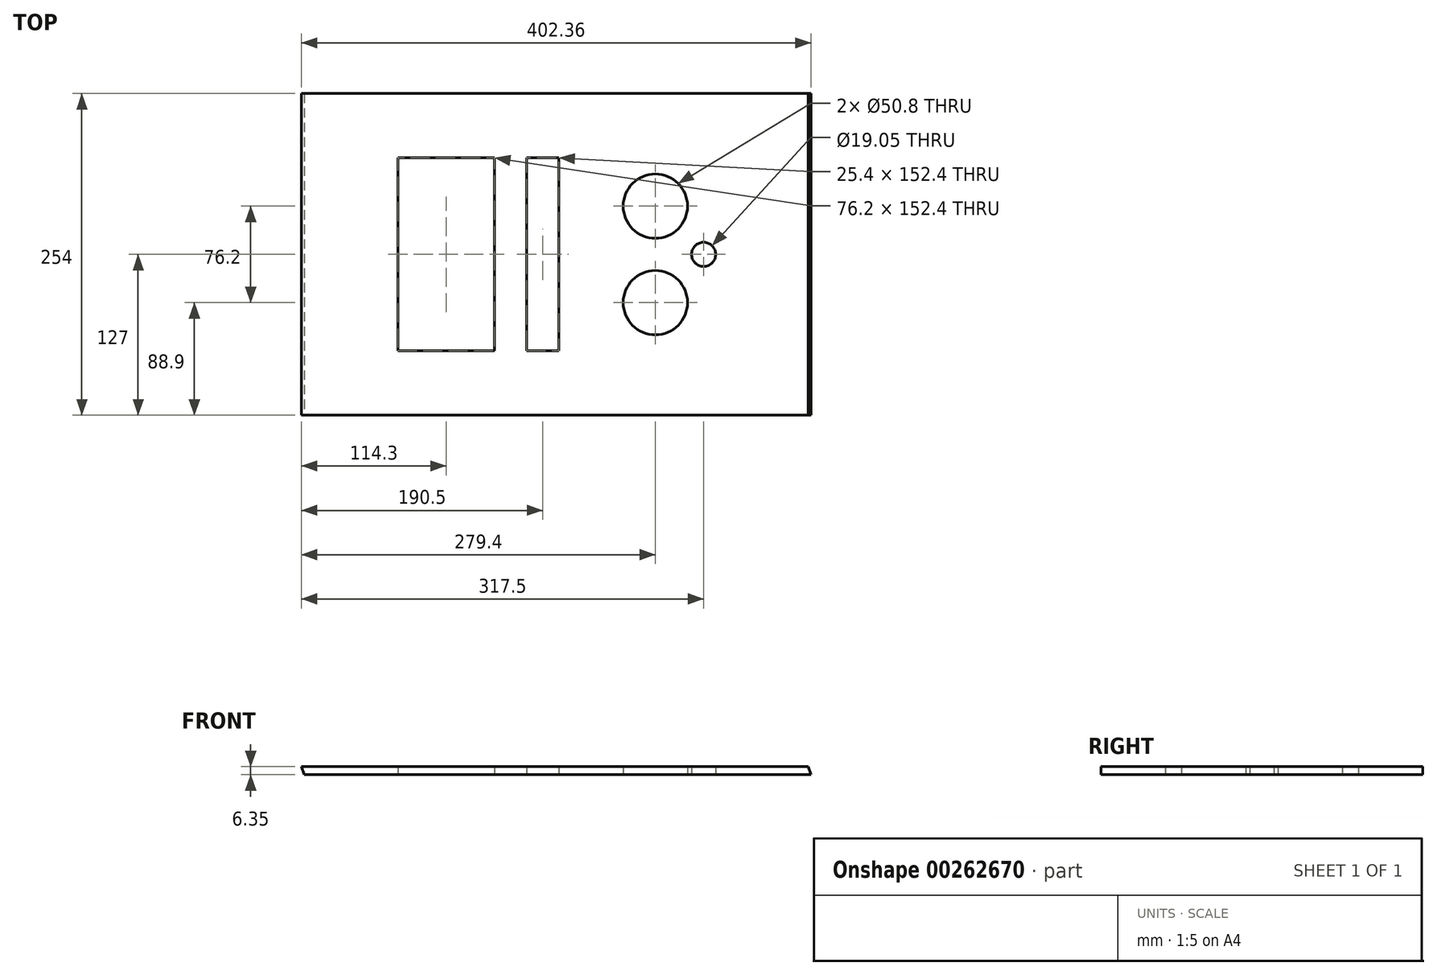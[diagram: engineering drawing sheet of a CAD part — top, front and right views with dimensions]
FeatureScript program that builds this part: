
annotation { "Feature Type Name" : "Feature", "Feature Type Description" : "" }
export const myFeature = defineFeature(function(context is Context, id is Id, definition is map)
    precondition{}
    {
        {
            var Q0;
            Q0=qCreatedBy(makeId("Top.planeOp"),FACE);
            var sketch = newSketch(context, id + "F0", { "sketchPlane" : qUnion([Q0])});
            skLineSegment(sketch, "E0.bottom", {"start": v(0, 0) * mm, "end": v(406.4, 0) * mm});
            skLineSegment(sketch, "E0.top", {"start": v(0, 254) * mm, "end": v(406.4, 254) * mm});
            skLineSegment(sketch, "E0.left", {"start": v(0, 0) * mm, "end": v(0, 254) * mm});
            skLineSegment(sketch, "E0.right", {"start": v(406.4, 0) * mm, "end": v(406.4, 254) * mm});
            skLineSegment(sketch, "E1.bottom", {"start": v(76.2, 203.2) * mm, "end": v(152.4, 203.2) * mm});
            skLineSegment(sketch, "E1.top", {"start": v(76.2, 50.8) * mm, "end": v(152.4, 50.8) * mm});
            skLineSegment(sketch, "E1.left", {"start": v(76.2, 203.2) * mm, "end": v(76.2, 50.8) * mm});
            skLineSegment(sketch, "E1.right", {"start": v(152.4, 203.2) * mm, "end": v(152.4, 50.8) * mm});
            skLineSegment(sketch, "E2.bottom", {"start": v(177.8, 203.2) * mm, "end": v(203.2, 203.2) * mm});
            skLineSegment(sketch, "E2.top", {"start": v(177.8, 50.8) * mm, "end": v(203.2, 50.8) * mm});
            skLineSegment(sketch, "E2.left", {"start": v(177.8, 203.2) * mm, "end": v(177.8, 50.8) * mm});
            skLineSegment(sketch, "E2.right", {"start": v(203.2, 203.2) * mm, "end": v(203.2, 50.8) * mm});
            skCircle(sketch, "E3", {"center": v(279.4, 88.9) * mm, "radius": 25.4 * mm});
            skCircle(sketch, "E4", {"center": v(279.4, 165.1) * mm, "radius": 25.4 * mm});
            skCircle(sketch, "E5", {"center": v(317.5, 127) * mm, "radius": 9.53 * mm});
            skPoint(sketch, "E5.centerSnap0", {"position": v(203.2, 127) * mm});
            skSolve(sketch);
        }
        {
            var Q0;
            Q0=makeQuery(id+"F0.imprint","IMPRINT",FACE,{"disambiguationData":[TD([[makeQuery(id+"F0.imprint","IMPRINT",EDGE,{"derivedFrom":sQuery(id+"F0.wireOp",EDGE,"E0.bottom")}),1.0]])]});
            extrude(context, id + "F1", {"entities" : qUnion([Q0]), "depth" : 6.35 * mm});
        }
        {
            var Q0;
            Q0=makeQuery(id+"F1.opExtrude","SWEPT_FACE",FACE,{"disambiguationData":[OSD([sQuery(id+"F0.wireOp",EDGE,"E0.bottom")])]});
            var sketch = newSketch(context, id + "F2", { "sketchPlane" : qUnion([Q0])});
            skLineSegment(sketch, "E6", {"start": v(-1.79, 11.26) * mm, "end": v(2.31, 0) * mm});
            skLineSegment(sketch, "E7", {"start": v(2.31, 0) * mm, "end": v(-1.79, 0) * mm});
            skLineSegment(sketch, "E8", {"start": v(-1.79, 0) * mm, "end": v(-1.79, 11.26) * mm});
            skSolve(sketch);
        }
        {
            var Q0;
            {var subQ1=sQuery(id+"F0.wireOp",EDGE,"E0.bottom");var subQ2=makeQuery(id+"F1.opExtrude","SWEPT_EDGE",EDGE,{"disambiguationData":[OSD([subQ1,sQuery(id+"F0.wireOp",EDGE,"E0.left")])]});Q0=makeQuery(id+"F2.imprint","IMPRINT",FACE,{"disambiguationData":[TD([[makeQuery(id+"F2.imprint","IMPRINT",EDGE,{"derivedFrom":subQ2}),1.0]])]});}
            extrude(context, id + "F3", {"entities" : qUnion([Q0]), "operationType" : NewBodyOperationType.REMOVE, "endBound" : BoundingType.THROUGH_ALL, "oppositeDirection" : true, "depth" : 25.4 * mm});
        }
        {
            var Q0;
            Q0=makeQuery(id+"F1.opExtrude","SWEPT_FACE",FACE,{"disambiguationData":[OSD([sQuery(id+"F0.wireOp",EDGE,"E0.bottom")])]});
            var sketch = newSketch(context, id + "F4", { "sketchPlane" : qUnion([Q0])});
            skLineSegment(sketch, "E9", {"start": v(2.31, 0) * mm, "end": v(402.36, 0) * mm});
            skLineSegment(sketch, "E10", {"start": v(402.36, 0) * mm, "end": v(396.66, 15.66) * mm});
            skLineSegment(sketch, "E11", {"start": v(396.66, 15.66) * mm, "end": v(417.73, 15.66) * mm});
            skLineSegment(sketch, "E12", {"start": v(417.73, 15.66) * mm, "end": v(417.73, 0) * mm});
            skLineSegment(sketch, "E13", {"start": v(417.73, 0) * mm, "end": v(402.36, 0) * mm});
            skSolve(sketch);
        }
        {
            var Q0;
            {var subQ3=sQuery(id+"F0.wireOp",EDGE,"E0.bottom");var subQ6=makeQuery(id+"F1.opExtrude","SWEPT_EDGE",EDGE,{"disambiguationData":[OSD([subQ3,sQuery(id+"F0.wireOp",EDGE,"E0.right")])]});Q0=makeQuery(id+"F4.imprint","IMPRINT",FACE,{"disambiguationData":[TD([[makeQuery(id+"F4.imprint","IMPRINT",EDGE,{"derivedFrom":subQ6}),-1.0]])]});}
            extrude(context, id + "F5", {"entities" : qUnion([Q0]), "operationType" : NewBodyOperationType.REMOVE, "endBound" : BoundingType.THROUGH_ALL, "oppositeDirection" : true, "depth" : 25.4 * mm});
        }
    });
